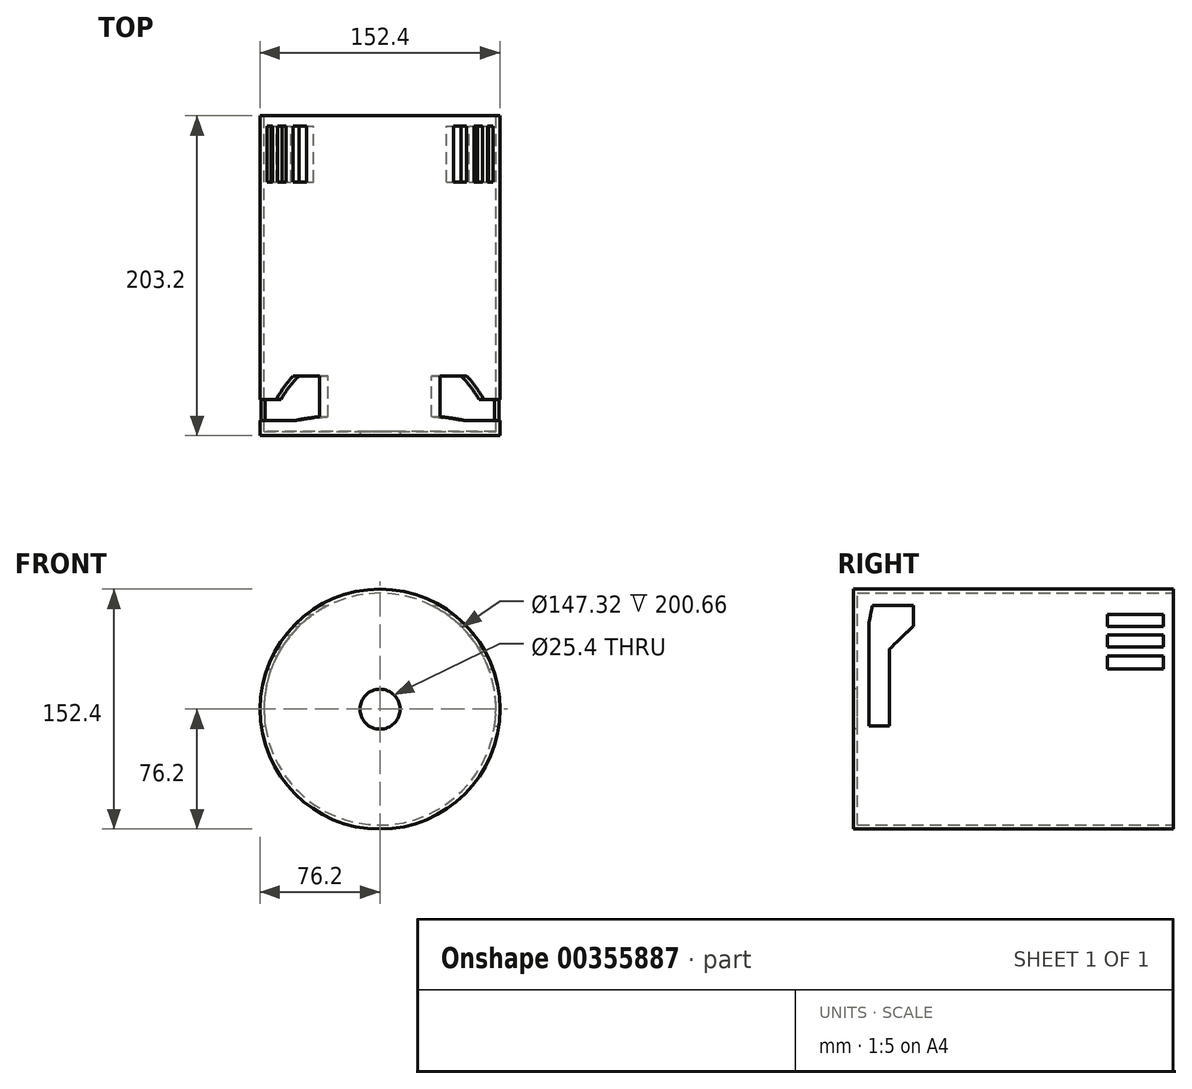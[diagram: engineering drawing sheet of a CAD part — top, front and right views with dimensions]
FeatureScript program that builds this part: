
annotation { "Feature Type Name" : "Feature", "Feature Type Description" : "" }
export const myFeature = defineFeature(function(context is Context, id is Id, definition is map)
    precondition{}
    {
        {
            var Q0;
            Q0=qCreatedBy(makeId("Front.planeOp"),FACE);
            var sketch = newSketch(context, id + "F0", { "sketchPlane" : qUnion([Q0])});
            skCircle(sketch, "E0", {"center": v(0, 0) * mm, "radius": 76.2 * mm});
            skSolve(sketch);
        }
        {
            var Q0;
            Q0=qSketchRegion(id+"F0",true);
            extrude(context, id + "F1", {"entities" : qUnion([Q0]), "depth" : 203.2 * mm});
        }
        {
            var Q0;
            Q0=makeQuery(id+"F1.opExtrude","CAP_FACE",FACE,{"disambiguationData":[OSD([sQuery(id+"F0.wireOp",EDGE,"E0")])],"isStart":false});
            var sketch = newSketch(context, id + "F2", { "sketchPlane" : qUnion([Q0])});
            skCircle(sketch, "E1", {"center": v(0, 0) * mm, "radius": 12.7 * mm});
            skSolve(sketch);
        }
        {
            var Q0;
            Q0=qSketchRegion(id+"F2",true);
            extrude(context, id + "F3", {"entities" : qUnion([Q0]), "operationType" : NewBodyOperationType.ADD, "depth" : 38.1 * mm});
        }
        {
            var Q0;
            Q0=makeQuery(id+"F1.opExtrude","CAP_FACE",FACE,{"disambiguationData":[OSD([sQuery(id+"F0.wireOp",EDGE,"E0")])],"isStart":true});
            shell(context, id + "F4", {"entities" : qUnion([Q0]), "thickness" : 2.54 * mm});
        }
        {
            var Q0;
            Q0=qCreatedBy(makeId("Right.planeOp"),FACE);
            var sketch = newSketch(context, id + "F5", { "sketchPlane" : qUnion([Q0])});
            skLineSegment(sketch, "E2", {"start": v(-191.12, 65.91) * mm, "end": v(-165.21, 65.91) * mm});
            skLineSegment(sketch, "E3", {"start": v(-165.21, 65.91) * mm, "end": v(-165.21, 52.67) * mm});
            skLineSegment(sketch, "E4", {"start": v(-165.21, 52.67) * mm, "end": v(-180.18, 38.28) * mm});
            skLineSegment(sketch, "E5", {"start": v(-180.18, 38.28) * mm, "end": v(-180.18, -10.65) * mm});
            skLineSegment(sketch, "E6", {"start": v(-180.18, -10.65) * mm, "end": v(-193.42, -10.65) * mm});
            skLineSegment(sketch, "E7", {"start": v(-193.42, -10.65) * mm, "end": v(-193.42, 54.4) * mm});
            skLineSegment(sketch, "E8", {"start": v(-193.42, 54.4) * mm, "end": v(-191.12, 65.91) * mm});
            skLineSegment(sketch, "E9.bottom", {"start": v(-6.46, 52.67) * mm, "end": v(-42.02, 52.67) * mm});
            skLineSegment(sketch, "E9.top", {"start": v(-6.46, 60.3) * mm, "end": v(-42.02, 60.3) * mm});
            skLineSegment(sketch, "E9.left", {"start": v(-6.46, 52.67) * mm, "end": v(-6.46, 60.3) * mm});
            skLineSegment(sketch, "E9.right", {"start": v(-42.02, 52.67) * mm, "end": v(-42.02, 60.3) * mm});
            skPoint(sketch, "E9.middle", {"position": v(-24.24, 56.48) * mm});
            skLineSegment(sketch, "E10.bottom", {"start": v(-6.46, 39.65) * mm, "end": v(-42.02, 39.65) * mm});
            skLineSegment(sketch, "E10.top", {"start": v(-6.46, 47.27) * mm, "end": v(-42.02, 47.27) * mm});
            skLineSegment(sketch, "E10.left", {"start": v(-6.46, 39.65) * mm, "end": v(-6.46, 47.27) * mm});
            skLineSegment(sketch, "E10.right", {"start": v(-42.02, 39.65) * mm, "end": v(-42.02, 47.27) * mm});
            skPoint(sketch, "E10.middle", {"position": v(-24.24, 43.46) * mm});
            skLineSegment(sketch, "E11.bottom", {"start": v(-6.46, 25.62) * mm, "end": v(-42.02, 25.62) * mm});
            skLineSegment(sketch, "E11.top", {"start": v(-6.46, 33.68) * mm, "end": v(-42.02, 33.68) * mm});
            skLineSegment(sketch, "E11.left", {"start": v(-6.46, 25.62) * mm, "end": v(-6.46, 33.68) * mm});
            skLineSegment(sketch, "E11.right", {"start": v(-42.02, 25.62) * mm, "end": v(-42.02, 33.68) * mm});
            skPoint(sketch, "E11.middle", {"position": v(-24.24, 29.65) * mm});
            skSolve(sketch);
        }
        {
            var Q0;
            Q0=makeQuery(id+"F5.imprint","IMPRINT",FACE,{"disambiguationData":[TD([[makeQuery(id+"F5.imprint","IMPRINT",EDGE,{"derivedFrom":sQuery(id+"F5.wireOp",EDGE,"E9.bottom")}),-1.0]])]});
            var Q1;
            Q1=makeQuery(id+"F5.imprint","IMPRINT",FACE,{"disambiguationData":[TD([[makeQuery(id+"F5.imprint","IMPRINT",EDGE,{"derivedFrom":sQuery(id+"F5.wireOp",EDGE,"E10.bottom")}),-1.0]])]});
            var Q2;
            Q2=makeQuery(id+"F5.imprint","IMPRINT",FACE,{"disambiguationData":[TD([[makeQuery(id+"F5.imprint","IMPRINT",EDGE,{"derivedFrom":sQuery(id+"F5.wireOp",EDGE,"E11.bottom")}),-1.0]])]});
            var Q3;
            Q3=makeQuery(id+"F5.imprint","IMPRINT",FACE,{"disambiguationData":[TD([[makeQuery(id+"F5.imprint","IMPRINT",EDGE,{"derivedFrom":sQuery(id+"F5.wireOp",EDGE,"E2")}),-1.0]])]});
            extrude(context, id + "F6", {"entities" : qUnion([Q0, Q1, Q2, Q3]), "operationType" : NewBodyOperationType.REMOVE, "endBound" : BoundingType.SYMMETRIC, "oppositeDirection" : true, "depth" : 177.8 * mm});
        }
        {
            var Q0;
            Q0=makeQuery(id+"F3.opExtrude","CAP_FACE",FACE,{"disambiguationData":[OSD([sQuery(id+"F2.wireOp",EDGE,"E1")])],"isStart":false});
            var sketch = newSketch(context, id + "F7", { "sketchPlane" : qUnion([Q0])});
            skSolve(sketch);
        }
        {
            var Q0;
            Q0=makeQuery(id+"F7.imprint","IMPRINT",FACE,{"disambiguationData":[TD([[makeQuery(id+"F7.imprint","IMPRINT",EDGE,{"derivedFrom":makeQuery(id+"F3.opExtrude","CAP_EDGE",EDGE,{"disambiguationData":[OSD([sQuery(id+"F2.wireOp",EDGE,"E1")])],"isStart":false})}),1.0]])]});
            extrude(context, id + "F8", {"entities" : qUnion([Q0]), "operationType" : NewBodyOperationType.REMOVE, "endBound" : BoundingType.THROUGH_ALL, "oppositeDirection" : true, "depth" : 25.4 * mm});
        }
    });
